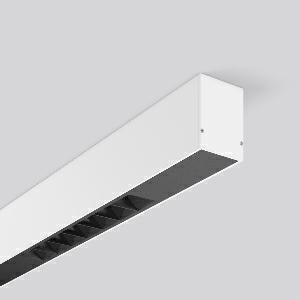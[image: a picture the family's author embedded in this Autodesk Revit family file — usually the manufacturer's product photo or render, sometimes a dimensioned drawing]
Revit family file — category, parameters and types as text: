
# Revit family: less_is_more_beamline_312483_002_15e1
name_source: partatom
category: Lighting Fixtures
units: mm (PartAtom-declared; Revit-internal decimal feet)

## family parameters
Cut with Voids When Loaded = No
Host = Face
Light Source = No
Part Type = Normal
Room Calculation Point = No
Round Connector Dimension = Use Diameter
Shared = No

## types (1)
- LESS IS MORE BEAMLINE (1 x LED Modul 930, 1025 lm, 3000)
    Apparent Load = 23 VA
    CIE Flux Codes = 100 100 100 100 100
    Color Rendering = 90
    Color Temperature = 3000
    Default Elevation = 1800 mm
    Description = Series: LESS IS MORE BEAMLINE
Linear ceiling and wall luminaire for aesthetically sophisticated lighting. Luminaire with two LED light units. Housing: extruded aluminium profile, powder-coated. End cap aluminium powder-coated. LED light unit with MRS technology: Mini-Reflector-System made of metallised thermoplastic with prismatic black glare-suppressing frame for pleasant glare-free light (RUG < 10). Each LED light unit has 7 reflector elements. Narrow beam light distribution. LED unit with integrated converter interchangeable and removable. Suitable for through-wiring. 
Colour: traffic white, matt (RAL 9016)
Length: 1127 mm
Width: 57 mm
Height: 75 mm
Lamp: LED
Socket: without socket
Colour temperature: 3000K
Colour rendering index (CRI): 90
System power: 23 W
Rated luminous flux: 2050 lm
Luminous efficiency: 89 lm/W
Control gear: Regulated power supply
Protection class: I
Type of protection: IP 20
    Height = 75 mm
    Lamp = 1 x LED Modul 930
    Lamp Light Flux = 1025 lm
    Lamp count = 1
    Length = 1127 mm
    Lifetime = 50000 h
    Luminous efficacy = 89 lm/W
    Manufacturer = RZB
    ModVariant = No
    Model = 312483.002
    Mounting Place = Ceiling, Wall
    Mounting Type = Surface mounted
    Number of Poles = 1
    OnlyDefault = Yes
    Power Factor = 1
    Product Name = LESS IS MORE BEAMLINE
    Product group = Surface mounted LED linear luminaires
    ProductGroupID = 307
    Protection Class = Protection class I
    Protection Degree = IP 20
    RLX_Detail_Level = 1
    RLX_Emergency_Light_Flux = 0 lm
    RLX_Emergency_Type = 0
    RLX_Emergency_Type_DB = No
    RlxData = <blob elided: 26953 chars, md5=8de289ae>
    Socket = socket
    Standby Power = 0 W
    System Light Flux = 2050 lm
    System Power = 23 W
    Type Comments = Product without accessories
    Type Image = 312483.002.jpg
    URL = http://relux.com
    VarID = ---
    Voltage = 230 V
    Voltage Range = 220-240 V
    Weight = 0.00 kg
    Width = 57 mm

## geometry (parser evidence)
native form markers: Blend x4, Sweep x17
no freeform markers — native parametric forms only
